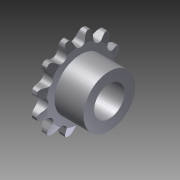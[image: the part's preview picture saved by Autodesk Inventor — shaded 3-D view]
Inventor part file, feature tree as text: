
AUTODESK INVENTOR PART (.ipt)
format: ipt  version: 2012 (Build 160160000, 160)  size: 355,840 bytes
history: native  units: in
note: dims shown in document units (in); Inventor stores cm internally (conversion verified against a paired STEP export)
features: sketch x2, revolve x1, extrude x1
ambient origin geometry x8: Origin, YZ Plane, XZ Plane, XY Plane, X Axis, Y Axis, Z Axis, Center Point
bodies: Solid1 (feature_tree)
feature tree (4):
  revolve  "Revolution1"  [1 undecoded]
  extrude  "Extrusion2"  Depth=0.3346in
  sketch  "Sketch1"  dims[d0=0.125in d1=0.1969in]
  sketch  "Sketch3"  dims[d3=0.55in d4=0.3346in d5=90.0deg d12=0.375in d26=30.0deg d27=0.0649in d29=4.7244in d30=0.0684in d31=0.483in d32=0.0469in d33=0.0684in d34=0.125in d35=360.0deg d36=0.25in d37=0.55in d38=1.1in d39=1.0in d40=0.0in]
note: 1 required parameter value undecoded (feature->parameter linkage not recoverable at this tier; creation-order binding heuristic only, values carry confidence <= 0.55)
